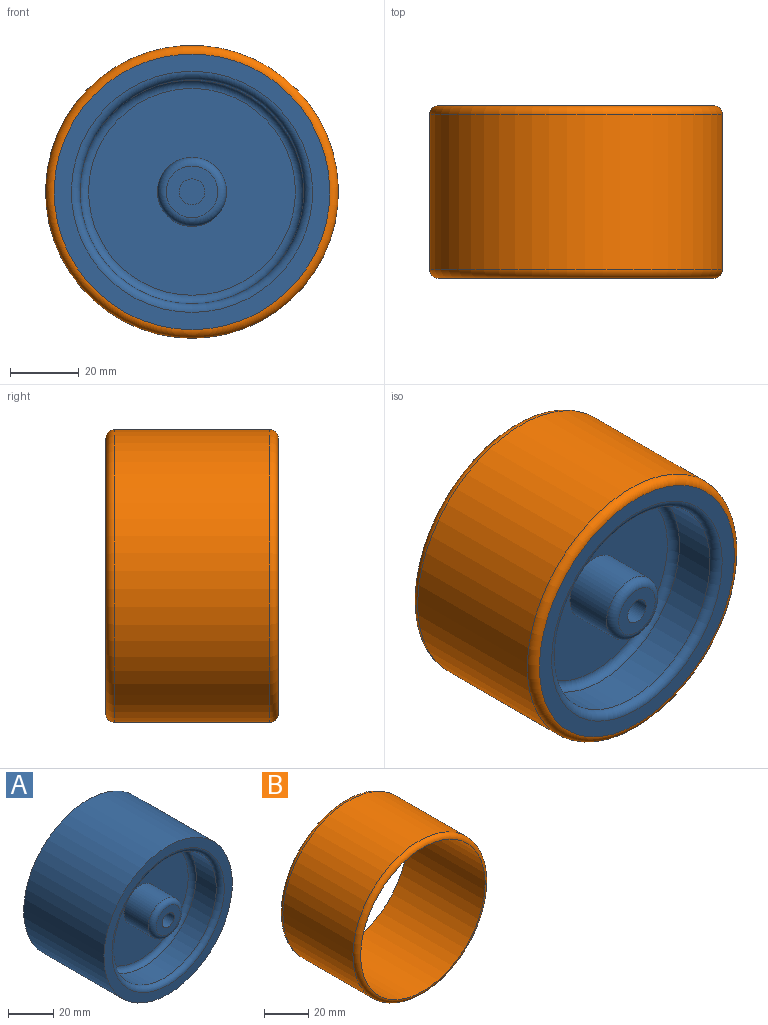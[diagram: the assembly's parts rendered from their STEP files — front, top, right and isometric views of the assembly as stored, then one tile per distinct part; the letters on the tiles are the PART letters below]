
ASSEMBLY  parts=2 mates=1
PART A: 23 faces, bbox 80x50x80 mm
  f0: cylinder r=40mm len=80mm, axis (0,1,0), area 12566.4mm2, adj f1,f2
  f1: plane 80x80mm, normal (0,-1,0), area 1178.1mm2, adj f0,f15
  f2: plane 80x80mm, normal (0,1,0), area 1178.1mm2, adj f0,f13
  f3: cylinder r=32.5mm len=65mm, axis (0,-1,0), area 2552.5mm2, adj f15,f16
  f4: plane 60x60mm, normal (0,-1,0), area 2513.3mm2, adj f9,f16
  f5: cylinder r=32.5mm len=65mm, axis (0,1,0), area 2552.5mm2, adj f13,f14
  f6: plane 60x60mm, normal (0,1,0), area 2513.3mm2, adj f8,f14
  f7: plane 15x15mm, normal (0,1,0), area 105.8mm2, adj f11,f21
  f8: cylinder r=10mm len=20mm, axis (0,1,0), area 942.5mm2, adj f6,f11
  f9: cylinder r=10mm len=20mm, axis (0,1,0), area 942.5mm2, adj f4,f12
  f10: plane 15x15mm, normal (0,-1,0), area 132.5mm2, adj f12,f19
  f11: torus R=7.5mm, axis (0,1,0), area 224.3mm2, adj f7,f8
  f12: torus R=7.5mm, axis (0,1,0), area 224.3mm2, adj f9,f10
  f13: torus R=35mm, axis (0,-1,0), area 824.3mm2, adj f2,f5
  f14: torus R=30mm, axis (0,1,0), area 779.5mm2, adj f5,f6
  f15: torus R=35mm, axis (0,-1,0), area 824.3mm2, adj f1,f3
  f16: torus R=30mm, axis (0,-1,0), area 779.5mm2, adj f3,f4
  f17: cylinder r=3.75mm len=18mm, axis (0,1,0), area 424.1mm2, adj f21,f22
  f18: plane 5.5x5.5mm, normal (0,1,0), area 23.8mm2, adj f22
  f19: cylinder r=3.75mm len=20mm, axis (0,-1,0), area 471.2mm2, adj f10,f20
  f20: plane 7.5x7.5mm, normal (0,-1,0), area 44.2mm2, adj f19
  f21: cone r=3.75mm half-angle=45deg, axis (0,1,0), area 37.8mm2, adj f7,f17
  f22: cone r=2.75mm half-angle=45deg, axis (0,1,0), area 28.9mm2, adj f17,f18
PART B: 4 faces, bbox 92x50x92 mm
  f0: cylinder r=42.5mm len=85mm, axis (0,1,0), area 12016.6mm2, adj f2,f3
  f1: cylinder r=40mm len=80mm, axis (0,-1,0), area 12566.4mm2, adj f2,f3
  f2: torus R=40mm, axis (0,-1,0), area 1026.2mm2, adj f0,f1
  f3: torus R=40mm, axis (0,-1,0), area 1026.2mm2, adj f0,f1
PLACE A t=(-32.43,-2.28,-12.83)mm
PLACE B t=(-32.43,-2.28,-12.83)mm
MATE fastened B.f1 <-> A.f8  axis (0,-1,0) through (-32.43,-52.28,-12.83)mm
